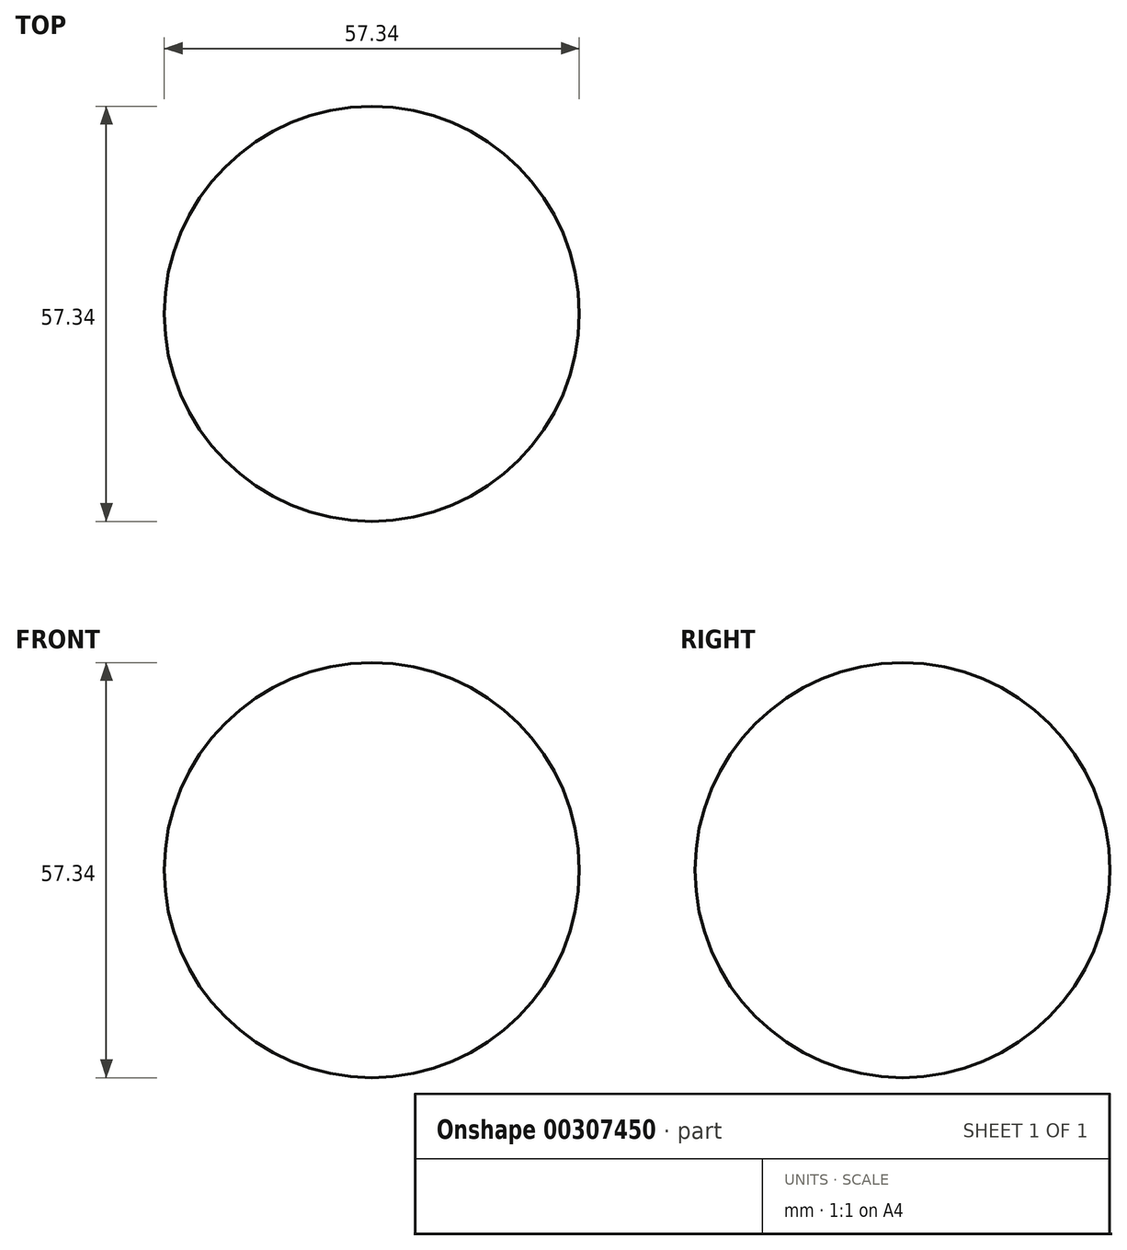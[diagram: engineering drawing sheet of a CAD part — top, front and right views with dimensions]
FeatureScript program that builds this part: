
annotation { "Feature Type Name" : "Feature", "Feature Type Description" : "" }
export const myFeature = defineFeature(function(context is Context, id is Id, definition is map)
    precondition{}
    {
        {
            var Q0;
            Q0=qCreatedBy(makeId("Front.planeOp"),FACE);
            var sketch = newSketch(context, id + "F0", { "sketchPlane" : qUnion([Q0])});
            skArc(sketch, "E0", {"start": v(0, 28.67) * mm, "mid": v(28.67, 0) * mm, "end": v(0, -28.67) * mm});
            skLineSegment(sketch, "E1", {"start": v(0, 28.67) * mm, "end": v(0, -28.67) * mm});
            skSolve(sketch);
        }
        {
            var Q0;
            Q0 = qSketchRegion(id + "F0", true);
            var Q1;
            Q1=sQuery(id+"F0.wireOp",EDGE,"E1");
            revolve(context, id + "F1", {"entities" : qUnion([Q0]), "axis" : qUnion([Q1]), "revolveType" : RevolveType.FULL});
        }
    });
